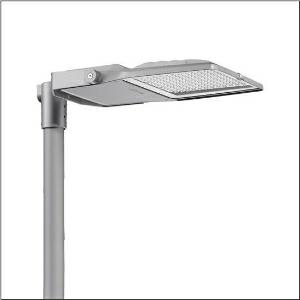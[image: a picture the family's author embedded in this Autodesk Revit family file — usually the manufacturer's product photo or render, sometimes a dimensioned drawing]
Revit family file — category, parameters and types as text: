
# Revit family: floodlight_fl_21_midi___pl52_5xa7786f4d3a_c4a6
name_source: partatom
category: Lighting Fixtures
units: mm (PartAtom-declared; Revit-internal decimal feet)

## family parameters
Cut with Voids When Loaded = No
Host = Face
Light Source = No
Part Type = Normal
Room Calculation Point = No
Round Connector Dimension = Use Diameter
Shared = No

## types (1)
- --- (1 x LED, 37330 lm, 271.6 W, 4000K)
    Apparent Load = 272 VA
    CIE Flux Codes = 26 60 98 100 100
    Color Rendering = 70
    Color Temperature = 4000K
    Default Elevation = 1800 mm
    Description = Floodlight FL 21 midi, floodlight, primary light control with lens, of PMMA, primary optical cover: protective disc, of toughened safety glass, transparent, light distribution: PL52, light emission: direct distribution, installation type: surface-mounted, LED, High Power LED, rated luminous flux: 37.330lm, luminous efficacy: 137lm/W, light colour: 740, colour temperature: 4000K, control gear: Smart Interface (Zhaga)D4i, control: overheat protection, constant luminous flux control, time-dependent luminous flux control, flexible luminous flux parameterisation, pre-setting: logarithmic dimming characteristic, with terminal, 6-pole, mains connection: 220..240V, AC, 50/60Hz, start of lifetime: 272W, end of service life: 287W, reduction: 123W, mast bracket, of diecast aluminium, powder-coated, SITECO metallic grey (DB 702S), corrosivity category C5 mid according to DIN EN ISO 12944, suitable for swimming pools, chlorine-resistant, sealing non-destructively replaceable, mast bracket, of steel, galvanised, powder-coated, SITECO metallic grey (DB 702S), Smart Interface below and above, protection rating (complete): IP66, insulation class (complete): insulation class II (safety insulation), certification: CE, ENEC, VDE, protection symbol: D, impact resistance: IK08, permissible operating ambient temperature: -40..+40°C, permissible operating ambient temperature for outdoor applications: -40..+50°C, standard: DIN EN 12944, LABS conformity tested according to VDMA 24364:2018-05, packaging unit: 1 piece

Light Distribution: PL52
    Height = 76 mm
    Lamp = 1 x LED
    Lamp Light Flux = 37330 lm
    Lamp Power = 271.6 W
    Lamp count = 1
    Length = 657 mm
    Luminous efficacy = 137 lm/W
    Manufacturer = Siteco
    ModVariant = No
    Model = 5XA7786F4D3A
    Number of Poles = 1
    OnlyDefault = Yes
    Power Factor = 1
    Product Name = Floodlight FL 21 midi | PL52
    Product group = floodlight | pylon annexe
    ProductGroupID = 6201
    Protection Class = Protection class II
    Protection Degree = IP 66
    RLX_Detail_Level = 1
    RLX_Emergency_Light_Flux = 0 lm
    RLX_Emergency_Type = 0
    RLX_Emergency_Type_DB = No
    RlxData = <blob elided: 104865 chars, md5=ce052d7f>
    Socket = socket
    Standby Power = 0 W
    System Light Flux = 37330 lm
    System Power = 272 W
    Type Comments = factory setting: luminous flux: 100 % | dim-lin: 254 | 620 mA
    Type Image = l_1007123.jpg
    URL = http://relux.com
    VarID = @adj_093107
    Voltage = 0 V
    Weight = 0.00 kg
    Width = 442 mm

## geometry (parser evidence)
native form markers: Blend x4, Sweep x14
no freeform markers — native parametric forms only
